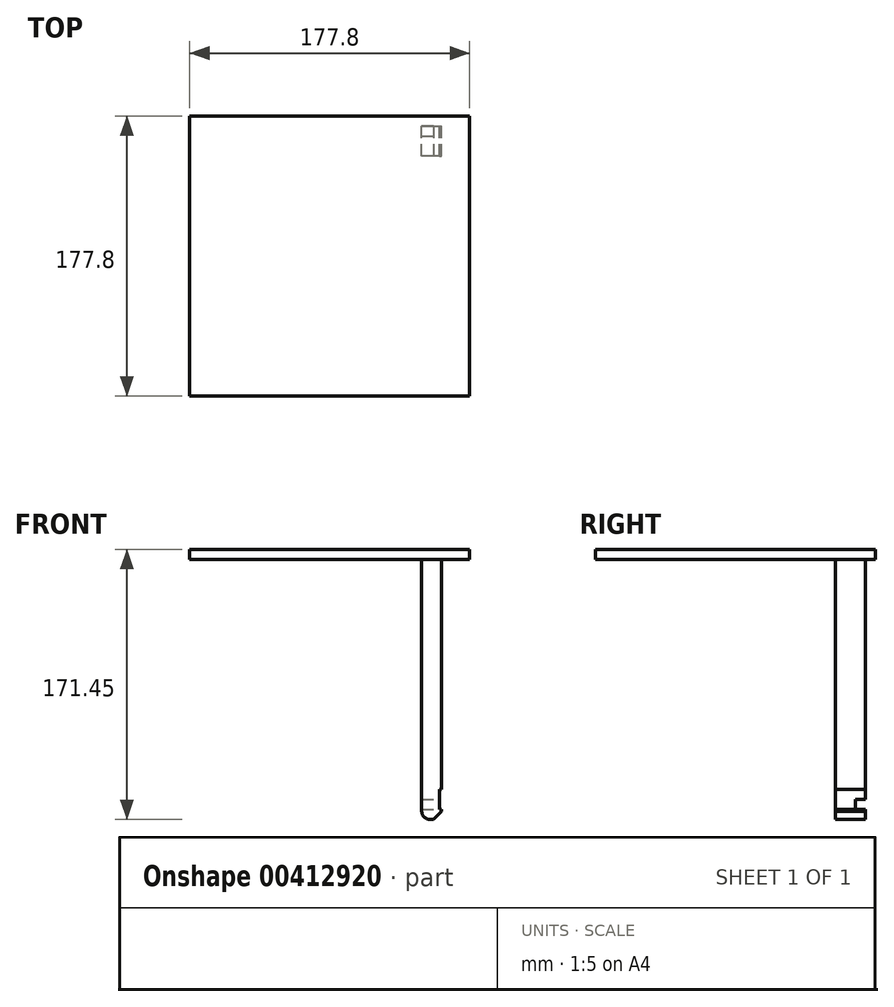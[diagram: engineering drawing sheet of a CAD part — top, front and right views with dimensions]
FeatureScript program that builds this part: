
annotation { "Feature Type Name" : "Feature", "Feature Type Description" : "" }
export const myFeature = defineFeature(function(context is Context, id is Id, definition is map)
    precondition{}
    {
        {
            var Q0;
            Q0=qCreatedBy(makeId("Top.planeOp"),FACE);
            cPlane(context, id + "F0", {"entities" : qUnion([Q0]), "cplaneType" : CPlaneType.OFFSET, "offset" : 177.8 * mm, "width" : 152.4 * mm, "height" : 152.4 * mm});
        }
        {
            var Q0;
            Q0=qCreatedBy(id+"F0.planeOp",FACE);
            var sketch = newSketch(context, id + "F1", { "sketchPlane" : qUnion([Q0])});
            skLineSegment(sketch, "E0.bottom", {"start": v(88.9, 88.9) * mm, "end": v(-88.9, 88.9) * mm});
            skLineSegment(sketch, "E0.top", {"start": v(88.9, -88.9) * mm, "end": v(-88.9, -88.9) * mm});
            skLineSegment(sketch, "E0.left", {"start": v(88.9, 88.9) * mm, "end": v(88.9, -88.9) * mm});
            skLineSegment(sketch, "E0.right", {"start": v(-88.9, 88.9) * mm, "end": v(-88.9, -88.9) * mm});
            skPoint(sketch, "E0.middle", {"position": v(0, 0) * mm});
            skSolve(sketch);
        }
        {
            var Q0;
            Q0=makeQuery(id+"F1.imprint","IMPRINT",FACE,{"disambiguationData":[TD([[makeQuery(id+"F1.imprint","IMPRINT",EDGE,{"derivedFrom":sQuery(id+"F1.wireOp",EDGE,"E0.bottom")}),1.0]])]});
            extrude(context, id + "F2", {"entities" : qUnion([Q0]), "depth" : 6.35 * mm});
        }
        {
            var Q0;
            Q0=makeQuery(id+"F2.opExtrude","CAP_FACE",FACE,{"disambiguationData":[OSD([sQuery(id+"F1.wireOp",EDGE,"E0.bottom"),sQuery(id+"F1.wireOp",EDGE,"E0.top"),sQuery(id+"F1.wireOp",EDGE,"E0.left"),sQuery(id+"F1.wireOp",EDGE,"E0.right")])],"isStart":true});
            var sketch = newSketch(context, id + "F3", { "sketchPlane" : qUnion([Q0])});
            skLineSegment(sketch, "E1.bottom", {"start": v(71.12, -63.5) * mm, "end": v(58.42, -63.5) * mm});
            skLineSegment(sketch, "E1.top", {"start": v(71.12, -82.55) * mm, "end": v(58.42, -82.55) * mm});
            skLineSegment(sketch, "E1.left", {"start": v(71.12, -63.5) * mm, "end": v(71.12, -82.55) * mm});
            skLineSegment(sketch, "E1.right", {"start": v(58.42, -63.5) * mm, "end": v(58.42, -82.55) * mm});
            skPoint(sketch, "E1.middle", {"position": v(64.77, -73.02) * mm});
            skSolve(sketch);
        }
        {
            var Q0;
            Q0=makeQuery(id+"F3.imprint","IMPRINT",FACE,{"disambiguationData":[TD([[makeQuery(id+"F3.imprint","IMPRINT",EDGE,{"derivedFrom":sQuery(id+"F3.wireOp",EDGE,"E1.bottom")}),1.0]])]});
            extrude(context, id + "F4", {"entities" : qUnion([Q0]), "operationType" : NewBodyOperationType.ADD, "depth" : 165.1 * mm});
        }
        {
            var Q0;
            Q0=makeQuery(id+"F4.opExtrude","SWEPT_FACE",FACE,{"disambiguationData":[OSD([sQuery(id+"F3.wireOp",EDGE,"E1.left")])]});
            var sketch = newSketch(context, id + "F5", { "sketchPlane" : qUnion([Q0])});
            skLineSegment(sketch, "E2.bottom", {"start": v(63.5, 19.05) * mm, "end": v(82.55, 19.05) * mm});
            skLineSegment(sketch, "E2.top", {"start": v(63.5, 31.75) * mm, "end": v(82.55, 31.75) * mm});
            skLineSegment(sketch, "E2.left", {"start": v(63.5, 19.05) * mm, "end": v(63.5, 31.75) * mm});
            skLineSegment(sketch, "E2.right", {"start": v(82.55, 19.05) * mm, "end": v(82.55, 31.75) * mm});
            skSolve(sketch);
        }
        {
            var Q0;
            Q0 = qSketchRegion(id + "F5", true);
            extrude(context, id + "F6", {"entities" : qUnion([Q0]), "operationType" : NewBodyOperationType.REMOVE, "oppositeDirection" : true, "depth" : 1.27 * mm});
        }
        {
            var Q0;
            Q0=makeQuery(id+"F4.opExtrude","CAP_EDGE",EDGE,{"disambiguationData":[OSD([sQuery(id+"F3.wireOp",EDGE,"E1.left")])],"isStart":false});
            chamfer(context, id + "F7", {"entities" : qUnion([Q0]), "width" : 5.08 * mm, "tangentPropagation" : true});
        }
        {
            var Q0;
            Q0=makeQuery(id+"F4.opExtrude","CAP_EDGE",EDGE,{"disambiguationData":[OSD([sQuery(id+"F3.wireOp",EDGE,"E1.right")])],"isStart":false});
            fillet(context, id + "F8", {"entities" : qUnion([Q0]), "radius" : 5.08 * mm, "tangentPropagation" : true, "allowEdgeOverflow" : false});
        }
        {
            var Q0;
            Q0=makeQuery(id+"F6.boolean.opBoolean","COPY",FACE,{"derivedFrom":makeQuery(id+"F6.opExtrude","CAP_FACE",FACE,{"disambiguationData":[OSD([sQuery(id+"F5.wireOp",EDGE,"E2.bottom"),sQuery(id+"F5.wireOp",EDGE,"E2.top"),sQuery(id+"F5.wireOp",EDGE,"E2.left"),sQuery(id+"F5.wireOp",EDGE,"E2.right")])],"isStart":false})});
            var sketch = newSketch(context, id + "F9", { "sketchPlane" : qUnion([Q0])});
            skLineSegment(sketch, "E3", {"start": v(82.55, 19.05) * mm, "end": v(76.2, 19.05) * mm});
            skLineSegment(sketch, "E4", {"start": v(76.2, 19.05) * mm, "end": v(76.2, 25.4) * mm});
            skLineSegment(sketch, "E5", {"start": v(76.2, 25.4) * mm, "end": v(82.55, 25.4) * mm});
            skSolve(sketch);
        }
        {
            var Q0;
            {var subQ0=sQuery(id+"F9.wireOp",EDGE,"E3");Q0=makeQuery(id+"F9.imprint","IMPRINT",FACE,{"disambiguationData":[TD([[makeQuery(id+"F9.imprint","IMPRINT",EDGE,{"derivedFrom":subQ0}),1.0]])]});}
            extrude(context, id + "F10", {"entities" : qUnion([Q0]), "operationType" : NewBodyOperationType.REMOVE, "oppositeDirection" : true, "depth" : 25.4 * mm});
        }
    });
